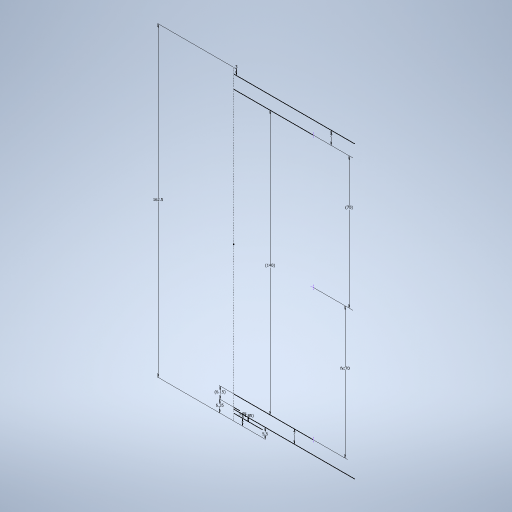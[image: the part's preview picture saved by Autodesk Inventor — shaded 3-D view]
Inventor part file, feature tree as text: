
AUTODESK INVENTOR PART (.ipt)
format: ipt  version: 2024 (Build 280153000, 153)  size: 245,760 bytes
history: native  units: mm
features: sketch x1
ambient origin geometry x8: Origin, YZ Plane, XZ Plane, XY Plane, X Axis, Y Axis, Z Axis, Center Point
feature tree (1):
  sketch  "Sketch1"  dims[d0=162.5mm d1=3.0mm d2=7.0mm d3=3.65mm d4=5.5mm d5=7.0mm d6=6.35mm d7=6.15mm d8=1.85mm d9=140.0mm d10=70.0mm d11=70.0mm]
